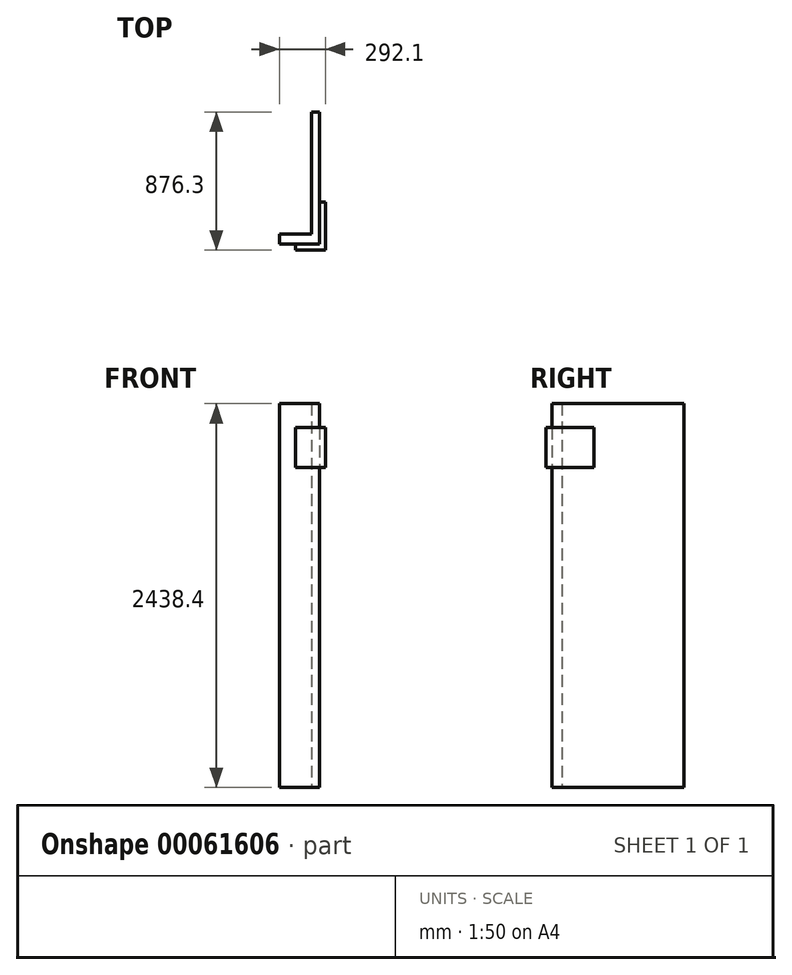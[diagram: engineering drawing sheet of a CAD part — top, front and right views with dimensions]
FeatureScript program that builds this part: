
annotation { "Feature Type Name" : "Feature", "Feature Type Description" : "" }
export const myFeature = defineFeature(function(context is Context, id is Id, definition is map)
    precondition{}
    {
        {
            var Q0;
            Q0=qCreatedBy(makeId("Right.planeOp"),FACE);
            var sketch = newSketch(context, id + "F0", { "sketchPlane" : qUnion([Q0])});
            skLineSegment(sketch, "E0.rect.bottom", {"start": v(419.1, 1219.2) * mm, "end": v(-419.1, 1219.2) * mm});
            skLineSegment(sketch, "E0.rect.top", {"start": v(419.1, -1219.2) * mm, "end": v(-419.1, -1219.2) * mm});
            skLineSegment(sketch, "E0.rect.left", {"start": v(419.1, 1219.2) * mm, "end": v(419.1, -1219.2) * mm});
            skLineSegment(sketch, "E0.rect.right", {"start": v(-419.1, 1219.2) * mm, "end": v(-419.1, -1219.2) * mm});
            skPoint(sketch, "E0.rect.middle", {"position": v(0, 0) * mm});
            skSolve(sketch);
        }
        {
            var Q0;
            Q0 = qSketchRegion(id + "F0", true);
            extrude(context, id + "F1", {"entities" : qUnion([Q0]), "depth" : 50.8 * mm});
        }
        {
            var Q0;
            Q0=makeQuery(id+"F1.opExtrude","CAP_FACE",FACE,{"disambiguationData":[OSD([sQuery(id+"F0.wireOp",EDGE,"E0.rect.bottom"),sQuery(id+"F0.wireOp",EDGE,"E0.rect.top"),sQuery(id+"F0.wireOp",EDGE,"E0.rect.left"),sQuery(id+"F0.wireOp",EDGE,"E0.rect.right")])],"isStart":true});
            var sketch = newSketch(context, id + "F2", { "sketchPlane" : qUnion([Q0])});
            skLineSegment(sketch, "E1.bottom", {"start": v(419.1, 1219.2) * mm, "end": v(355.6, 1219.2) * mm});
            skLineSegment(sketch, "E1.top", {"start": v(419.1, -1219.2) * mm, "end": v(355.6, -1219.2) * mm});
            skLineSegment(sketch, "E1.left", {"start": v(419.1, 1219.2) * mm, "end": v(419.1, -1219.2) * mm});
            skLineSegment(sketch, "E1.right", {"start": v(355.6, 1219.2) * mm, "end": v(355.6, -1219.2) * mm});
            skSolve(sketch);
        }
        {
            var Q0;
            Q0 = qSketchRegion(id + "F2", true);
            extrude(context, id + "F3", {"entities" : qUnion([Q0]), "operationType" : NewBodyOperationType.ADD, "depth" : 203.2 * mm});
        }
        {
            var Q0;
            Q0=makeQuery(id+"F3.boolean.opBoolean","MERGE",FACE,{"derivedFrom":[makeQuery(id+"F1.opExtrude","SWEPT_FACE",FACE,{"disambiguationData":[OSD([sQuery(id+"F0.wireOp",EDGE,"E0.rect.right")])]}),makeQuery(id+"F3.opExtrude","SWEPT_FACE",FACE,{"disambiguationData":[OSD([sQuery(id+"F2.wireOp",EDGE,"E1.left")])]})]});
            var sketch = newSketch(context, id + "F4", { "sketchPlane" : qUnion([Q0])});
            skLineSegment(sketch, "E2.bottom", {"start": v(50.8, 1066.8) * mm, "end": v(-101.6, 1066.8) * mm});
            skLineSegment(sketch, "E2.top", {"start": v(50.8, 812.8) * mm, "end": v(-101.6, 812.8) * mm});
            skLineSegment(sketch, "E2.left", {"start": v(50.8, 1066.8) * mm, "end": v(50.8, 812.8) * mm});
            skLineSegment(sketch, "E2.right", {"start": v(-101.6, 1066.8) * mm, "end": v(-101.6, 812.8) * mm});
            skSolve(sketch);
        }
        {
            var Q0;
            Q0 = qSketchRegion(id + "F4", true);
            extrude(context, id + "F5", {"entities" : qUnion([Q0]), "operationType" : NewBodyOperationType.ADD, "depth" : 38.1 * mm});
        }
        {
            var Q0;
            Q0=makeQuery(id+"F5.boolean.opBoolean","MERGE",FACE,{"derivedFrom":[makeQuery(id+"F1.opExtrude","CAP_FACE",FACE,{"disambiguationData":[OSD([sQuery(id+"F0.wireOp",EDGE,"E0.rect.bottom"),sQuery(id+"F0.wireOp",EDGE,"E0.rect.top"),sQuery(id+"F0.wireOp",EDGE,"E0.rect.left"),sQuery(id+"F0.wireOp",EDGE,"E0.rect.right")])],"isStart":false}),makeQuery(id+"F5.opExtrude","SWEPT_FACE",FACE,{"disambiguationData":[OSD([sQuery(id+"F4.wireOp",EDGE,"E2.left")])]})]});
            var sketch = newSketch(context, id + "F6", { "sketchPlane" : qUnion([Q0])});
            skLineSegment(sketch, "E3.bottom", {"start": v(-457.2, 1066.8) * mm, "end": v(-152.4, 1066.8) * mm});
            skLineSegment(sketch, "E3.top", {"start": v(-457.2, 812.8) * mm, "end": v(-152.4, 812.8) * mm});
            skLineSegment(sketch, "E3.left", {"start": v(-457.2, 1066.8) * mm, "end": v(-457.2, 812.8) * mm});
            skLineSegment(sketch, "E3.right", {"start": v(-152.4, 1066.8) * mm, "end": v(-152.4, 812.8) * mm});
            skSolve(sketch);
        }
        {
            var Q0;
            Q0 = qSketchRegion(id + "F6", true);
            extrude(context, id + "F7", {"entities" : qUnion([Q0]), "operationType" : NewBodyOperationType.ADD, "depth" : 38.1 * mm});
        }
    });
